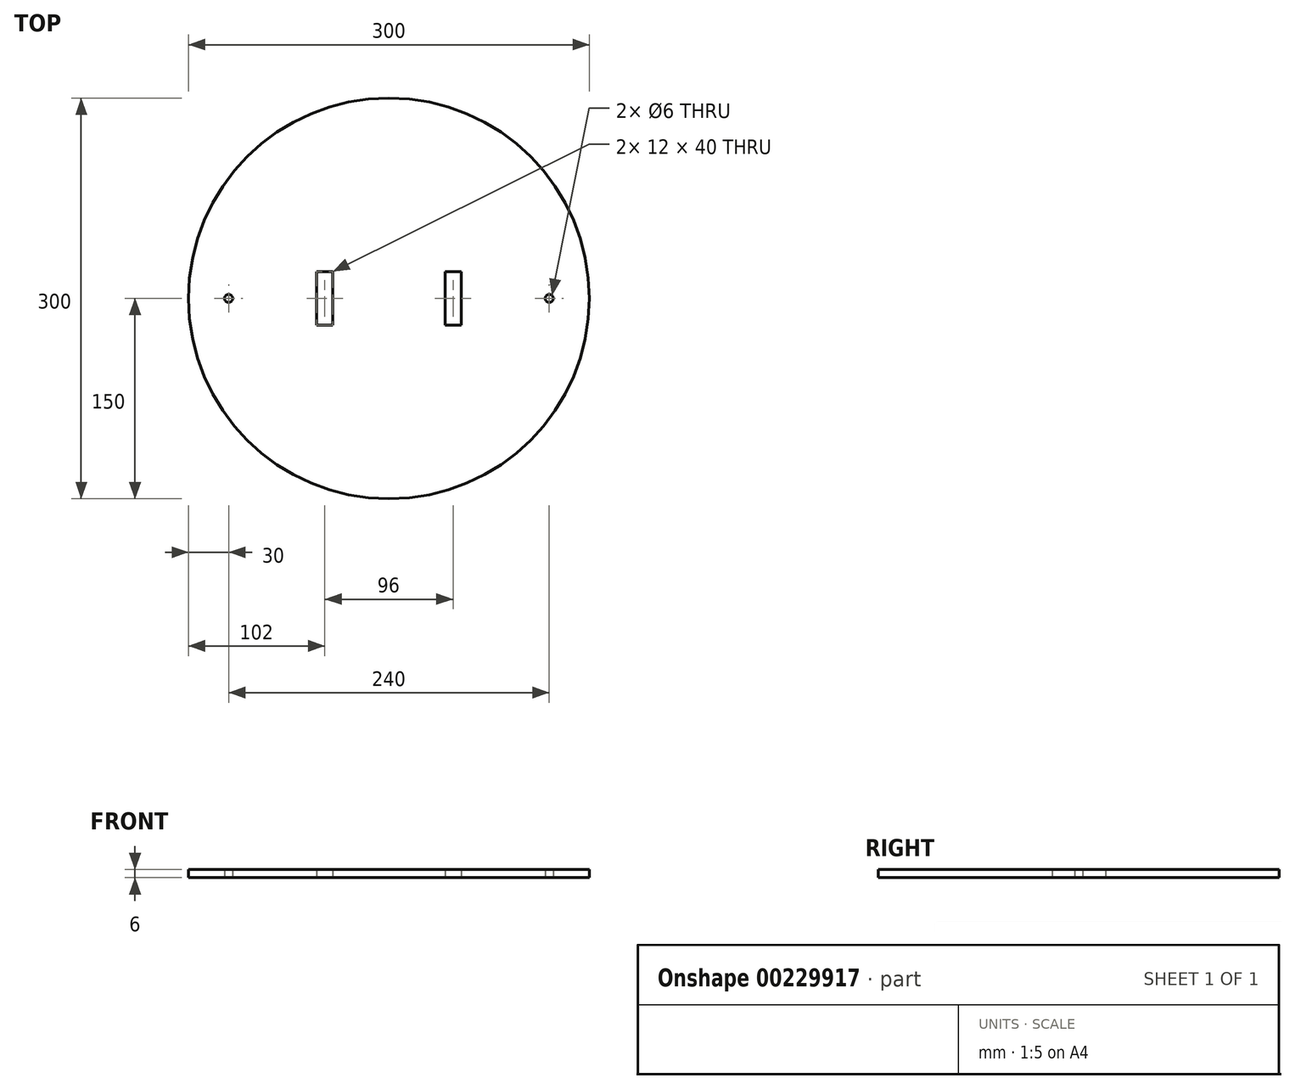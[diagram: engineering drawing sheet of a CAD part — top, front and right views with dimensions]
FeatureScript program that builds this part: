
annotation { "Feature Type Name" : "Feature", "Feature Type Description" : "" }
export const myFeature = defineFeature(function(context is Context, id is Id, definition is map)
    precondition{}
    {
        {
            var Q0;
            Q0=qCreatedBy(makeId("Top.planeOp"),FACE);
            var sketch = newSketch(context, id + "F0", { "sketchPlane" : qUnion([Q0])});
            skCircle(sketch, "E0", {"center": v(0, 0) * mm, "radius": 150 * mm});
            skLineSegment(sketch, "E1", {"start": v(0, 0) * mm, "end": v(0, 45.78) * mm, "construction": true});
            skLineSegment(sketch, "E2", {"start": v(-48, 47.51) * mm, "end": v(-48, -65.98) * mm, "construction": true});
            skLineSegment(sketch, "E3", {"start": v(32, 48.96) * mm, "end": v(32, -54.95) * mm, "construction": true});
            skLineSegment(sketch, "E4", {"start": v(0, 0) * mm, "end": v(-58.64, 0) * mm, "construction": true});
            skLineSegment(sketch, "E5", {"start": v(0, 0) * mm, "end": v(53.1, 0) * mm, "construction": true});
            skLineSegment(sketch, "E6.bottom", {"start": v(-54, 20) * mm, "end": v(-42, 20) * mm});
            skLineSegment(sketch, "E6.top", {"start": v(-54, -20) * mm, "end": v(-42, -20) * mm});
            skLineSegment(sketch, "E6.left", {"start": v(-54, 20) * mm, "end": v(-54, -20) * mm});
            skLineSegment(sketch, "E6.right", {"start": v(-42, 20) * mm, "end": v(-42, -20) * mm});
            skLineSegment(sketch, "E7.MirrorCS", {"start": v(42, 20) * mm, "end": v(42, -20) * mm});
            skLineSegment(sketch, "E8.MirrorCS", {"start": v(54, 20) * mm, "end": v(54, -20) * mm});
            skLineSegment(sketch, "E9.MirrorCS", {"start": v(54, -20) * mm, "end": v(42, -20) * mm});
            skLineSegment(sketch, "E10.MirrorCS", {"start": v(54, 20) * mm, "end": v(42, 20) * mm});
            skCircle(sketch, "E11", {"center": v(-120, 0) * mm, "radius": 3 * mm});
            skCircle(sketch, "E12.MirrorC", {"center": v(120, 0) * mm, "radius": 3 * mm});
            skSolve(sketch);
        }
        {
            var Q0;
            Q0 = qSketchRegion(id + "F0", true);
            extrude(context, id + "F1", {"entities" : qUnion([Q0]), "endBound" : BoundingType.SYMMETRIC, "depth" : 6 * mm});
        }
    });
